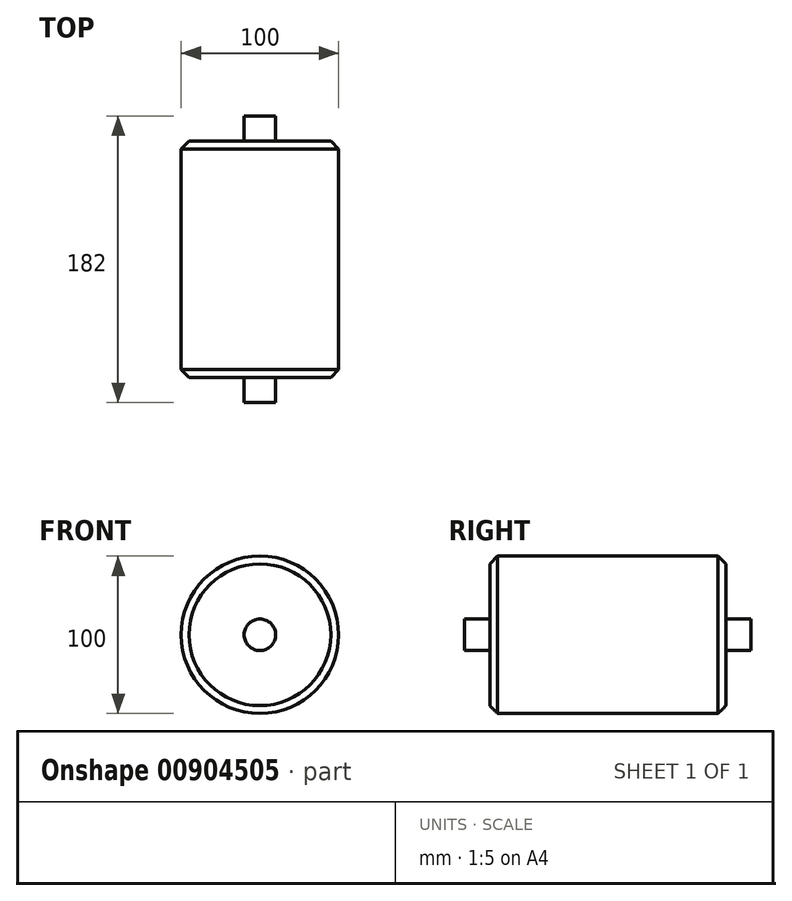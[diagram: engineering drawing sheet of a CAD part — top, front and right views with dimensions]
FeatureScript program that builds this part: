
annotation { "Feature Type Name" : "Feature", "Feature Type Description" : "" }
export const myFeature = defineFeature(function(context is Context, id is Id, definition is map)
    precondition{}
    {
        {
            var Q0;
            Q0=qCreatedBy(makeId("Front.planeOp"),FACE);
            var sketch = newSketch(context, id + "F0", { "sketchPlane" : qUnion([Q0])});
            skCircle(sketch, "E0", {"center": v(0, 0) * mm, "radius": 50 * mm});
            skSolve(sketch);
        }
        {
            var Q0;
            Q0=makeQuery(id+"F0.imprint","IMPRINT",FACE,{"disambiguationData":[TD([[makeQuery(id+"F0.imprint","IMPRINT",EDGE,{"derivedFrom":sQuery(id+"F0.wireOp",EDGE,"E0")}),1.0]])]});
            extrude(context, id + "F1", {"entities" : qUnion([Q0]), "depth" : 75 * mm, "offsetDistance" : 25.4 * mm});
        }
        {
            var Q0;
            Q0=makeQuery(id+"F1.opExtrude","CAP_FACE",FACE,{"disambiguationData":[OSD([sQuery(id+"F0.wireOp",EDGE,"E0")])],"isStart":true});
            extrude(context, id + "F2", {"entities" : qUnion([Q0]), "operationType" : NewBodyOperationType.ADD, "depth" : 75 * mm, "offsetDistance" : 25.4 * mm});
        }
        {
            var Q0;
            Q0=makeQuery(id+"F2.opExtrude","CAP_EDGE",EDGE,{"disambiguationData":[OSD([sQuery(id+"F0.wireOp",EDGE,"E0")])],"isStart":false});
            var Q1;
            Q1=makeQuery(id+"F1.opExtrude","CAP_EDGE",EDGE,{"disambiguationData":[OSD([sQuery(id+"F0.wireOp",EDGE,"E0")])],"isStart":false});
            chamfer(context, id + "F3", {"entities" : qUnion([Q0, Q1]), "width" : 5 * mm, "tangentPropagation" : true});
        }
        {
            var Q0;
            Q0=makeQuery(id+"F1.opExtrude","CAP_FACE",FACE,{"disambiguationData":[OSD([sQuery(id+"F0.wireOp",EDGE,"E0")])],"isStart":false});
            var sketch = newSketch(context, id + "F4", { "sketchPlane" : qUnion([Q0])});
            skCircle(sketch, "E1", {"center": v(0, 0) * mm, "radius": 10 * mm});
            skSolve(sketch);
        }
        {
            var Q0;
            Q0=makeQuery(id+"F4.imprint","IMPRINT",FACE,{"disambiguationData":[TD([[makeQuery(id+"F4.imprint","IMPRINT",EDGE,{"derivedFrom":sQuery(id+"F4.wireOp",EDGE,"E1")}),1.0]])]});
            extrude(context, id + "F5", {"entities" : qUnion([Q0]), "operationType" : NewBodyOperationType.ADD, "depth" : 16 * mm, "offsetDistance" : 25.4 * mm});
        }
        {
            var Q0;
            Q0=makeQuery(id+"F2.opExtrude","CAP_FACE",FACE,{"disambiguationData":[OSD([sQuery(id+"F0.wireOp",EDGE,"E0")])],"isStart":false});
            var sketch = newSketch(context, id + "F6", { "sketchPlane" : qUnion([Q0])});
            skCircle(sketch, "E2", {"center": v(0, 0) * mm, "radius": 10 * mm});
            skSolve(sketch);
        }
        {
            var Q0;
            Q0=makeQuery(id+"F6.imprint","IMPRINT",FACE,{"disambiguationData":[TD([[makeQuery(id+"F6.imprint","IMPRINT",EDGE,{"derivedFrom":sQuery(id+"F6.wireOp",EDGE,"E2")}),1.0]])]});
            extrude(context, id + "F7", {"entities" : qUnion([Q0]), "operationType" : NewBodyOperationType.ADD, "depth" : 16 * mm, "offsetDistance" : 25.4 * mm});
        }
    });
